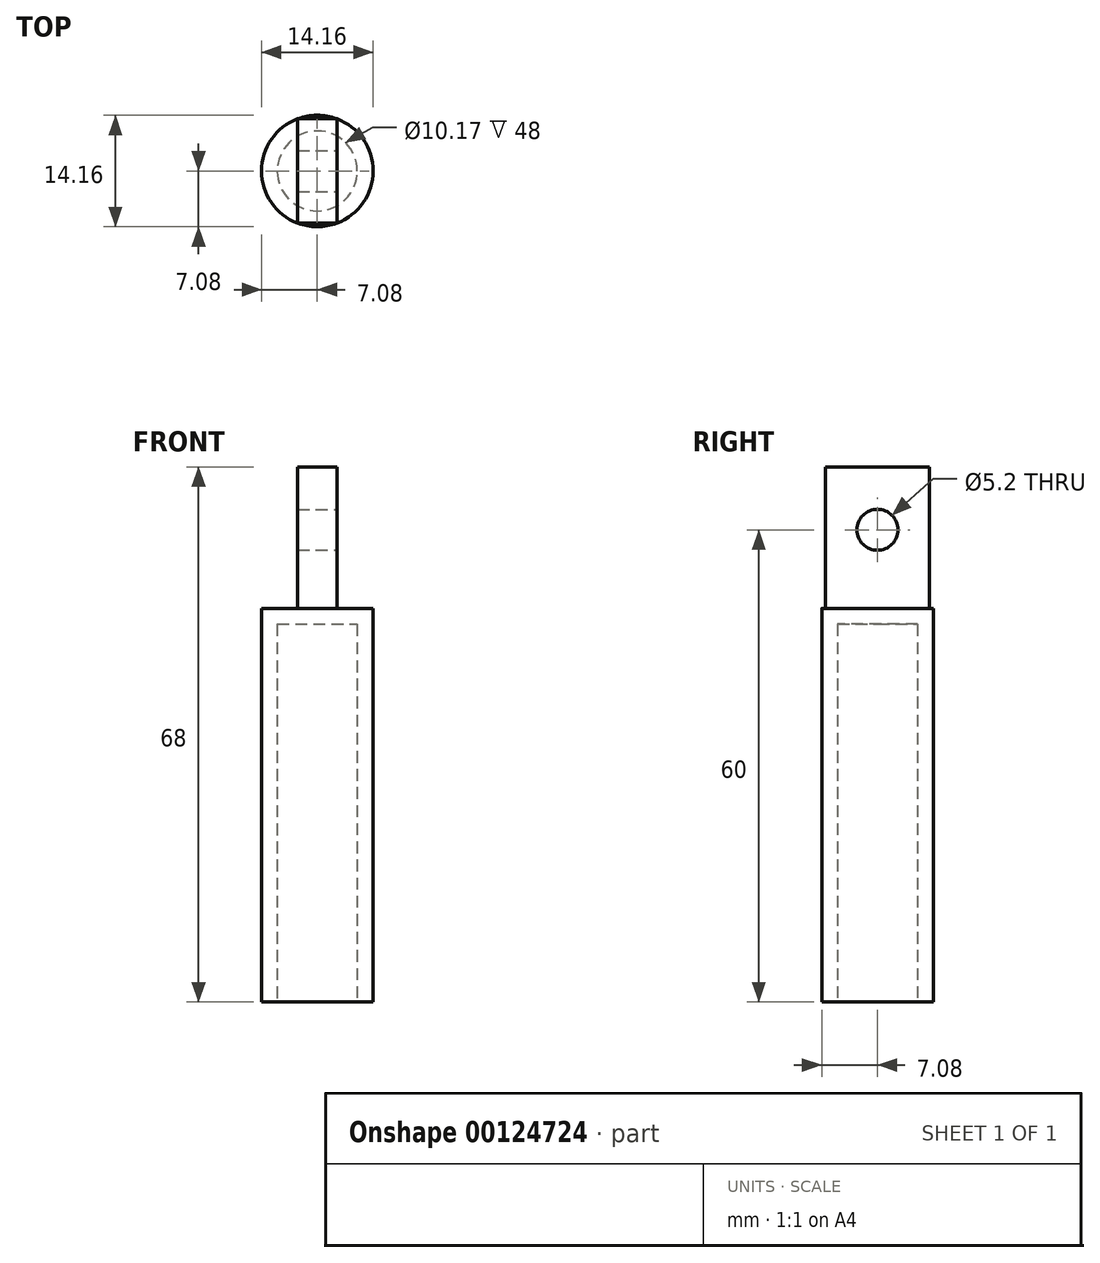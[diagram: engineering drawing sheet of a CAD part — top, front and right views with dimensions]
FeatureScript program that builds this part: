
annotation { "Feature Type Name" : "Feature", "Feature Type Description" : "" }
export const myFeature = defineFeature(function(context is Context, id is Id, definition is map)
    precondition{}
    {
        {
            var Q0;
            Q0=qCreatedBy(makeId("Top.planeOp"),FACE);
            var sketch = newSketch(context, id + "F0", { "sketchPlane" : qUnion([Q0])});
            skCircle(sketch, "E0", {"center": v(0, 0) * mm, "radius": 7.08 * mm});
            skLineSegment(sketch, "E1.bottom", {"start": v(-2.5, 6.63) * mm, "end": v(2.5, 6.63) * mm});
            skLineSegment(sketch, "E1.top", {"start": v(-2.5, -6.63) * mm, "end": v(2.5, -6.63) * mm});
            skLineSegment(sketch, "E1.left", {"start": v(-2.5, 6.63) * mm, "end": v(-2.5, -6.63) * mm});
            skLineSegment(sketch, "E1.right", {"start": v(2.5, 6.63) * mm, "end": v(2.5, -6.63) * mm});
            skSolve(sketch);
        }
        {
            var Q0;
            Q0 = qSketchRegion(id + "F0", true);
            extrude(context, id + "F1", {"entities" : qUnion([Q0]), "depth" : 50 * mm});
        }
        {
            var Q0;
            Q0=makeQuery(id+"F0.imprint","IMPRINT",FACE,{"disambiguationData":[TD([[makeQuery(id+"F0.imprint","IMPRINT",EDGE,{"derivedFrom":sQuery(id+"F0.wireOp",EDGE,"E1.bottom")}),-1.0]])]});
            extrude(context, id + "F2", {"entities" : qUnion([Q0]), "operationType" : NewBodyOperationType.ADD, "depth" : 68 * mm});
        }
        {
            var Q0;
            Q0=makeQuery(id+"F2.opExtrude","SWEPT_FACE",FACE,{"disambiguationData":[OSD([sQuery(id+"F0.wireOp",EDGE,"E1.right")])]});
            var sketch = newSketch(context, id + "F3", { "sketchPlane" : qUnion([Q0])});
            skCircle(sketch, "E2", {"center": v(0, 60) * mm, "radius": 2.6 * mm});
            skSolve(sketch);
        }
        {
            var Q0;
            Q0 = qSketchRegion(id + "F3", true);
            extrude(context, id + "F4", {"entities" : qUnion([Q0]), "operationType" : NewBodyOperationType.REMOVE, "endBound" : BoundingType.THROUGH_ALL, "oppositeDirection" : true, "depth" : 25 * mm});
        }
        {
            var Q0;
            Q0=makeQuery(id+"F1.opExtrude","CAP_FACE",FACE,{"disambiguationData":[OSD([sQuery(id+"F0.wireOp",EDGE,"E0")])],"isStart":true});
            var sketch = newSketch(context, id + "F5", { "sketchPlane" : qUnion([Q0])});
            skCircle(sketch, "E3", {"center": v(0, 0) * mm, "radius": 5.08 * mm});
            skSolve(sketch);
        }
        {
            var Q0;
            Q0 = qSketchRegion(id + "F5", true);
            extrude(context, id + "F6", {"entities" : qUnion([Q0]), "operationType" : NewBodyOperationType.REMOVE, "oppositeDirection" : true, "depth" : 48 * mm});
        }
    });
